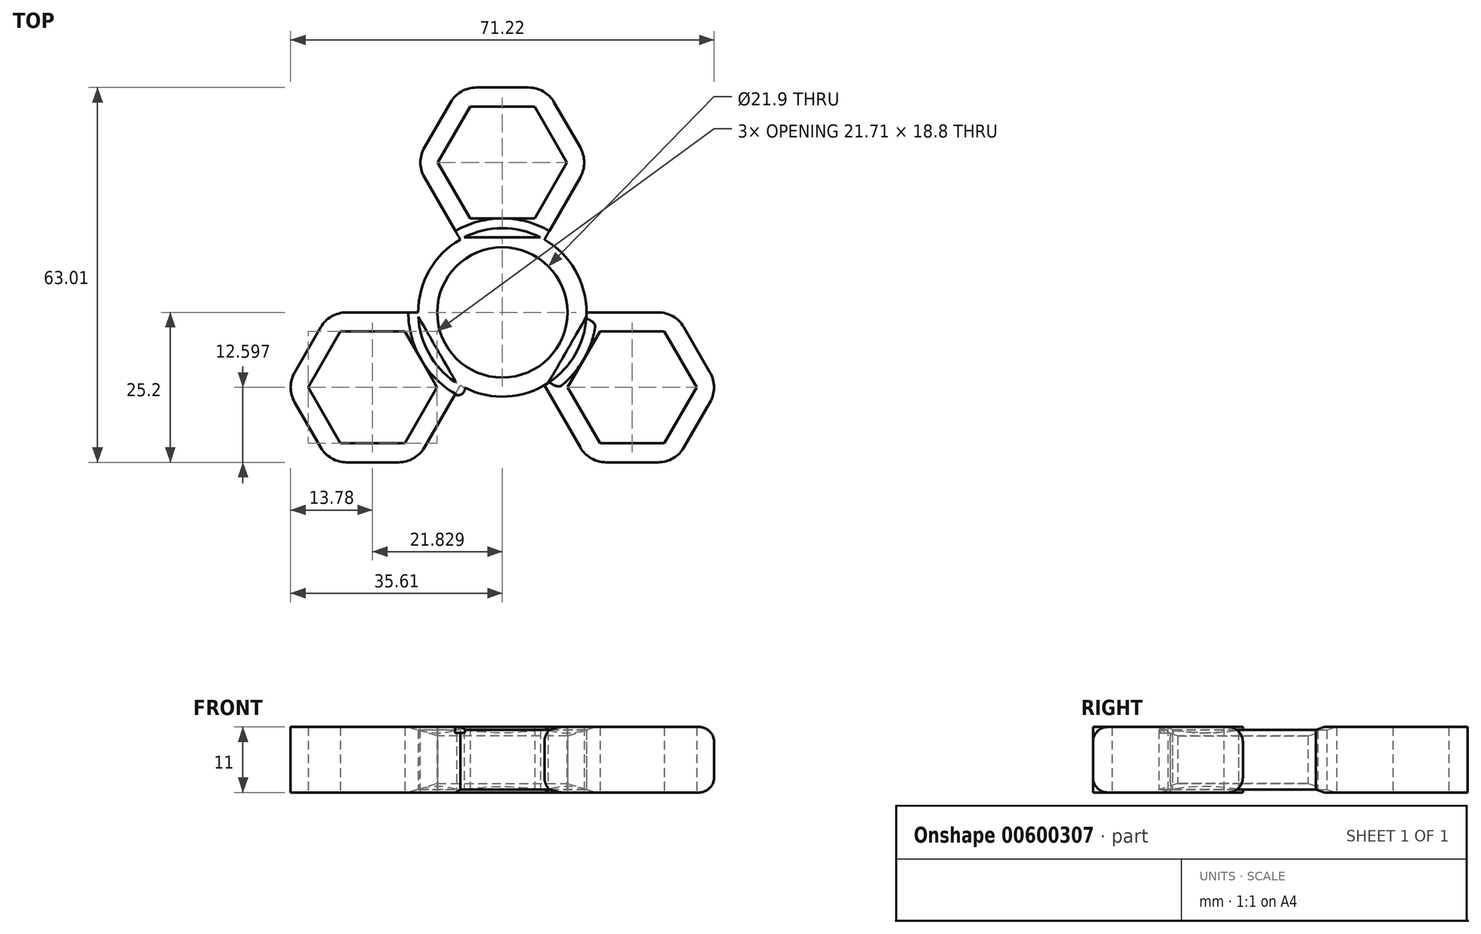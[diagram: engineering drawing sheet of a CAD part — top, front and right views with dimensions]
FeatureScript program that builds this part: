
annotation { "Feature Type Name" : "Feature", "Feature Type Description" : "" }
export const myFeature = defineFeature(function(context is Context, id is Id, definition is map)
    precondition{}
    {
        {
            var Q0;
            Q0=qCreatedBy(makeId("Top.planeOp"),FACE);
            var sketch = newSketch(context, id + "F0", { "sketchPlane" : qUnion([Q0])});
            skCircle(sketch, "E0", {"center": v(0, 0) * mm, "radius": 38.5 * mm, "construction": true});
            skLineSegment(sketch, "E1", {"start": v(0, 25.2) * mm, "end": v(0, 0) * mm, "construction": true});
            skLineSegment(sketch, "E2", {"start": v(0, 0) * mm, "end": v(-21.83, -12.6) * mm, "construction": true});
            skLineSegment(sketch, "E3", {"start": v(0, 0) * mm, "end": v(21.83, -12.6) * mm, "construction": true});
            skCircle(sketch, "E4.cCircle", {"center": v(0, 25.2) * mm, "radius": 9.4 * mm, "construction": true});
            skLineSegment(sketch, "E4.0", {"start": v(10.85, 25.2) * mm, "end": v(5.43, 15.8) * mm});
            skLineSegment(sketch, "E4.1", {"start": v(5.43, 15.8) * mm, "end": v(-5.43, 15.8) * mm});
            skLineSegment(sketch, "E4.2", {"start": v(-5.43, 15.8) * mm, "end": v(-10.85, 25.2) * mm});
            skLineSegment(sketch, "E4.3", {"start": v(-10.85, 25.2) * mm, "end": v(-5.43, 34.6) * mm});
            skLineSegment(sketch, "E4.4", {"start": v(-5.43, 34.6) * mm, "end": v(5.43, 34.6) * mm});
            skLineSegment(sketch, "E4.5", {"start": v(5.43, 34.6) * mm, "end": v(10.85, 25.2) * mm});
            skPoint(sketch, "E4.0.midPoint", {"position": v(8.14, 20.5) * mm});
            skCircle(sketch, "E5.cCircle", {"center": v(0, 25.2) * mm, "radius": 12.6 * mm, "construction": true});
            skLineSegment(sketch, "E5.0", {"start": v(14.55, 25.2) * mm, "end": v(7.27, 12.6) * mm});
            skLineSegment(sketch, "E5.1", {"start": v(7.27, 12.6) * mm, "end": v(-7.27, 12.6) * mm});
            skLineSegment(sketch, "E5.2", {"start": v(-7.27, 12.6) * mm, "end": v(-14.55, 25.2) * mm});
            skLineSegment(sketch, "E5.3", {"start": v(-14.55, 25.2) * mm, "end": v(-7.27, 37.8) * mm});
            skLineSegment(sketch, "E5.4", {"start": v(-7.27, 37.8) * mm, "end": v(7.27, 37.8) * mm});
            skLineSegment(sketch, "E5.5", {"start": v(7.27, 37.8) * mm, "end": v(14.55, 25.2) * mm});
            skPoint(sketch, "E5.0.midPoint", {"position": v(10.91, 18.9) * mm});
            skLineSegment(sketch, "E6", {"start": v(-7.27, 12.6) * mm, "end": v(-7.07, 12.26) * mm});
            skLineSegment(sketch, "E7", {"start": v(7.27, 12.6) * mm, "end": v(7.07, 12.26) * mm});
            skCircle(sketch, "E8", {"center": v(0, 0) * mm, "radius": 10.95 * mm});
            skCircle(sketch, "E9.cCircle", {"center": v(21.83, -12.6) * mm, "radius": 9.4 * mm, "construction": true});
            skLineSegment(sketch, "E9.0", {"start": v(32.68, -12.6) * mm, "end": v(27.26, -22) * mm});
            skLineSegment(sketch, "E9.1", {"start": v(27.26, -22) * mm, "end": v(16.4, -22) * mm});
            skLineSegment(sketch, "E9.2", {"start": v(16.4, -22) * mm, "end": v(10.98, -12.6) * mm});
            skLineSegment(sketch, "E9.3", {"start": v(10.98, -12.6) * mm, "end": v(16.4, -3.2) * mm});
            skLineSegment(sketch, "E9.4", {"start": v(16.4, -3.2) * mm, "end": v(27.26, -3.2) * mm});
            skLineSegment(sketch, "E9.5", {"start": v(27.26, -3.2) * mm, "end": v(32.68, -12.6) * mm});
            skPoint(sketch, "E9.0.midPoint", {"position": v(29.97, -17.3) * mm});
            skCircle(sketch, "E10.cCircle", {"center": v(21.83, -12.6) * mm, "radius": 12.6 * mm, "construction": true});
            skLineSegment(sketch, "E10.0", {"start": v(36.38, -12.6) * mm, "end": v(29.1, -25.2) * mm});
            skLineSegment(sketch, "E10.1", {"start": v(29.1, -25.2) * mm, "end": v(14.55, -25.2) * mm});
            skLineSegment(sketch, "E10.2", {"start": v(14.55, -25.2) * mm, "end": v(7.28, -12.6) * mm});
            skLineSegment(sketch, "E10.3", {"start": v(7.28, -12.6) * mm, "end": v(14.55, 0) * mm});
            skLineSegment(sketch, "E10.4", {"start": v(14.55, 0) * mm, "end": v(29.1, 0) * mm});
            skLineSegment(sketch, "E10.5", {"start": v(29.1, 0) * mm, "end": v(36.38, -12.6) * mm});
            skPoint(sketch, "E10.0.midPoint", {"position": v(32.74, -18.9) * mm});
            skCircle(sketch, "E11.cCircle", {"center": v(-21.83, -12.6) * mm, "radius": 9.4 * mm, "construction": true});
            skLineSegment(sketch, "E11.0", {"start": v(-10.98, -12.6) * mm, "end": v(-16.4, -22) * mm});
            skLineSegment(sketch, "E11.1", {"start": v(-16.4, -22) * mm, "end": v(-27.26, -22) * mm});
            skLineSegment(sketch, "E11.2", {"start": v(-27.26, -22) * mm, "end": v(-32.68, -12.6) * mm});
            skLineSegment(sketch, "E11.3", {"start": v(-32.68, -12.6) * mm, "end": v(-27.26, -3.2) * mm});
            skLineSegment(sketch, "E11.4", {"start": v(-27.26, -3.2) * mm, "end": v(-16.4, -3.2) * mm});
            skLineSegment(sketch, "E11.5", {"start": v(-16.4, -3.2) * mm, "end": v(-10.98, -12.6) * mm});
            skPoint(sketch, "E11.0.midPoint", {"position": v(-13.69, -17.3) * mm});
            skCircle(sketch, "E12.cCircle", {"center": v(-21.83, -12.6) * mm, "radius": 12.6 * mm, "construction": true});
            skLineSegment(sketch, "E12.0", {"start": v(-7.28, -12.6) * mm, "end": v(-14.55, -25.2) * mm});
            skLineSegment(sketch, "E12.1", {"start": v(-14.55, -25.2) * mm, "end": v(-29.1, -25.2) * mm});
            skLineSegment(sketch, "E12.2", {"start": v(-29.1, -25.2) * mm, "end": v(-36.38, -12.6) * mm});
            skLineSegment(sketch, "E12.3", {"start": v(-36.38, -12.6) * mm, "end": v(-29.1, 0) * mm});
            skLineSegment(sketch, "E12.4", {"start": v(-29.1, 0) * mm, "end": v(-14.55, 0) * mm});
            skLineSegment(sketch, "E12.5", {"start": v(-14.55, 0) * mm, "end": v(-7.28, -12.6) * mm});
            skPoint(sketch, "E12.0.midPoint", {"position": v(-10.92, -18.9) * mm});
            skLineSegment(sketch, "E13", {"start": v(-14.55, 0) * mm, "end": v(-14.15, 0) * mm});
            skLineSegment(sketch, "E14", {"start": v(-7.28, -12.6) * mm, "end": v(-7.08, -12.25) * mm});
            skLineSegment(sketch, "E15", {"start": v(7.28, -12.6) * mm, "end": v(7.08, -12.25) * mm});
            skLineSegment(sketch, "E16", {"start": v(14.55, 0) * mm, "end": v(14.15, 0) * mm});
            skCircle(sketch, "E17", {"center": v(0, 0) * mm, "radius": 14.15 * mm});
            skSolve(sketch);
        }
        {
            var Q0;
            Q0=qSketchRegion(id+"F0",true);
            extrude(context, id + "F1", {"entities" : qUnion([Q0]), "endBound" : BoundingType.SYMMETRIC, "depth" : 11 * mm, "offsetDistance" : 25 * mm});
        }
        {
            var Q0;
            Q0=makeQuery(id+"F1.opExtrude","CAP_FACE",FACE,{"disambiguationData":[OSD([sQuery(id+"F0.wireOp",EDGE,"E4.0"),sQuery(id+"F0.wireOp",EDGE,"E4.1"),sQuery(id+"F0.wireOp",EDGE,"E4.2"),sQuery(id+"F0.wireOp",EDGE,"E4.3"),sQuery(id+"F0.wireOp",EDGE,"E4.4"),sQuery(id+"F0.wireOp",EDGE,"E4.5"),sQuery(id+"F0.wireOp",EDGE,"E5.0"),sQuery(id+"F0.wireOp",EDGE,"E5.2"),sQuery(id+"F0.wireOp",EDGE,"E5.3"),sQuery(id+"F0.wireOp",EDGE,"E5.4"),sQuery(id+"F0.wireOp",EDGE,"E5.5"),sQuery(id+"F0.wireOp",EDGE,"E8"),sQuery(id+"F0.wireOp",EDGE,"E9.0"),sQuery(id+"F0.wireOp",EDGE,"E9.1"),sQuery(id+"F0.wireOp",EDGE,"E9.2"),sQuery(id+"F0.wireOp",EDGE,"E9.3"),sQuery(id+"F0.wireOp",EDGE,"E9.4"),sQuery(id+"F0.wireOp",EDGE,"E9.5"),sQuery(id+"F0.wireOp",EDGE,"E10.0"),sQuery(id+"F0.wireOp",EDGE,"E10.1"),sQuery(id+"F0.wireOp",EDGE,"E10.2"),sQuery(id+"F0.wireOp",EDGE,"E10.4"),sQuery(id+"F0.wireOp",EDGE,"E10.5"),sQuery(id+"F0.wireOp",EDGE,"E11.0"),sQuery(id+"F0.wireOp",EDGE,"E11.1"),sQuery(id+"F0.wireOp",EDGE,"E11.2"),sQuery(id+"F0.wireOp",EDGE,"E11.3"),sQuery(id+"F0.wireOp",EDGE,"E11.4"),sQuery(id+"F0.wireOp",EDGE,"E11.5"),sQuery(id+"F0.wireOp",EDGE,"E12.0"),sQuery(id+"F0.wireOp",EDGE,"E12.1"),sQuery(id+"F0.wireOp",EDGE,"E12.2"),sQuery(id+"F0.wireOp",EDGE,"E12.3"),sQuery(id+"F0.wireOp",EDGE,"E12.4"),sQuery(id+"F0.wireOp",EDGE,"E17")])],"isStart":false});
            var sketch = newSketch(context, id + "F2", { "sketchPlane" : qUnion([Q0])});
            skCircle(sketch, "E18", {"center": v(-7.49, -12.72) * mm, "radius": 1.2 * mm});
            skSolve(sketch);
        }
        {
            var Q0;
            Q0 = qSketchRegion(id + "F2", true);
            extrude(context, id + "F3", {"entities" : qUnion([Q0]), "operationType" : NewBodyOperationType.ADD, "oppositeDirection" : true, "depth" : 1 * mm, "offsetDistance" : 25 * mm});
        }
        {
            var Q0;
            Q0=qCreatedBy(makeId("Right.planeOp"),FACE);
            var sketch = newSketch(context, id + "F4", { "sketchPlane" : qUnion([Q0])});
            skLineSegment(sketch, "E19", {"start": v(-10.95, -5.5) * mm, "end": v(-10.95, 5.5) * mm, "construction": true});
            skLineSegment(sketch, "E20", {"start": v(10.95, 5.5) * mm, "end": v(10.95, -5.5) * mm, "construction": true});
            skLineSegment(sketch, "E21.0.0", {"start": v(15.8, -5.5) * mm, "end": v(25.2, -5.5) * mm, "construction": true});
            skLineSegment(sketch, "E21.0.1", {"start": v(25.2, -5.5) * mm, "end": v(25.2, 5.5) * mm, "construction": true});
            skLineSegment(sketch, "E21.0.2", {"start": v(25.2, 5.5) * mm, "end": v(15.8, 5.5) * mm, "construction": true});
            skLineSegment(sketch, "E21.0.3", {"start": v(15.8, 5.5) * mm, "end": v(15.8, -5.5) * mm, "construction": true});
            skLineSegment(sketch, "E22", {"start": v(10.95, 4) * mm, "end": v(15.8, 5.5) * mm});
            skLineSegment(sketch, "E23", {"start": v(15.8, 5.5) * mm, "end": v(10.95, 5.5) * mm});
            skLineSegment(sketch, "E24", {"start": v(10.95, 5.5) * mm, "end": v(10.95, 4) * mm});
            skLineSegment(sketch, "E25", {"start": v(10.95, -4) * mm, "end": v(10.95, -5.5) * mm});
            skLineSegment(sketch, "E26", {"start": v(10.95, -5.5) * mm, "end": v(15.8, -5.5) * mm});
            skLineSegment(sketch, "E27", {"start": v(15.8, -5.5) * mm, "end": v(10.95, -4) * mm});
            skLineSegment(sketch, "E28", {"start": v(0, 0) * mm, "end": v(0, 13.53) * mm, "construction": true});
            skSolve(sketch);
        }
        {
            var Q0;
            Q0=qSketchRegion(id+"F4",true);
            var Q1;
            Q1=sQuery(id+"F4.wireOp",EDGE,"E28");
            revolve(context, id + "F5", {"operationType" : NewBodyOperationType.REMOVE, "surfaceOperationType" : NewSurfaceOperationType.NEW, "entities" : qUnion([Q0]), "axis" : qUnion([Q1]), "revolveType" : RevolveType.FULL, "oppositeDirection" : true});
        }
        {
            var Q0;
            Q0=makeQuery(id+"F3.boolean.opBoolean","MERGE",EDGE,{"derivedFrom":[makeQuery(id+"F1.opExtrude","SWEPT_EDGE",EDGE,{"disambiguationData":[OSD([sQuery(id+"F0.wireOp",EDGE,"E10.4"),sQuery(id+"F0.wireOp",EDGE,"E10.5")])]}),makeQuery(id+"FbIfJMkWUXHlg3o_1.1.F1.opExtrude","SWEPT_EDGE",EDGE,{"disambiguationData":[OSD([sQuery(id+"F0.wireOp",EDGE,"E12.3"),sQuery(id+"F0.wireOp",EDGE,"E12.4")])]})]});
            var Q1;
            Q1=makeQuery(id+"FbIfJMkWUXHlg3o_1.1.F1.opExtrude","SWEPT_EDGE",EDGE,{"disambiguationData":[OSD([sQuery(id+"F0.wireOp",EDGE,"E12.2"),sQuery(id+"F0.wireOp",EDGE,"E12.3")])]});
            var Q2;
            Q2=makeQuery(id+"FbIfJMkWUXHlg3o_1.1.F1.opExtrude","SWEPT_EDGE",EDGE,{"disambiguationData":[OSD([sQuery(id+"F0.wireOp",EDGE,"E12.1"),sQuery(id+"F0.wireOp",EDGE,"E12.2")])]});
            var Q3;
            Q3=makeQuery(id+"F3.boolean.opBoolean","MERGE",EDGE,{"derivedFrom":[makeQuery(id+"F1.opExtrude","SWEPT_EDGE",EDGE,{"disambiguationData":[OSD([sQuery(id+"F0.wireOp",EDGE,"E5.0"),sQuery(id+"F0.wireOp",EDGE,"E5.5")])]}),makeQuery(id+"FbIfJMkWUXHlg3o_1.1.F1.opExtrude","SWEPT_EDGE",EDGE,{"disambiguationData":[OSD([sQuery(id+"F0.wireOp",EDGE,"E12.0"),sQuery(id+"F0.wireOp",EDGE,"E12.1")])]})]});
            var Q4;
            Q4=makeQuery(id+"F1.opExtrude","SWEPT_EDGE",EDGE,{"disambiguationData":[OSD([sQuery(id+"F0.wireOp",EDGE,"E5.4"),sQuery(id+"F0.wireOp",EDGE,"E5.5")])]});
            var Q5;
            Q5=makeQuery(id+"F1.opExtrude","SWEPT_EDGE",EDGE,{"disambiguationData":[OSD([sQuery(id+"F0.wireOp",EDGE,"E5.3"),sQuery(id+"F0.wireOp",EDGE,"E5.4")])]});
            var Q6;
            Q6=makeQuery(id+"FbIfJMkWUXHlg3o_1.1.F1.opExtrude","SWEPT_EDGE",EDGE,{"disambiguationData":[OSD([sQuery(id+"F0.wireOp",EDGE,"E10.0"),sQuery(id+"F0.wireOp",EDGE,"E10.1")])]});
            var Q7;
            Q7=makeQuery(id+"F3.boolean.opBoolean","MERGE",EDGE,{"derivedFrom":[makeQuery(id+"F1.opExtrude","SWEPT_EDGE",EDGE,{"disambiguationData":[OSD([sQuery(id+"F0.wireOp",EDGE,"E5.2"),sQuery(id+"F0.wireOp",EDGE,"E5.3")])]}),makeQuery(id+"FbIfJMkWUXHlg3o_1.1.F1.opExtrude","SWEPT_EDGE",EDGE,{"disambiguationData":[OSD([sQuery(id+"F0.wireOp",EDGE,"E10.1"),sQuery(id+"F0.wireOp",EDGE,"E10.2")])]})]});
            var Q8;
            Q8=makeQuery(id+"FbIfJMkWUXHlg3o_1.1.F1.opExtrude","SWEPT_EDGE",EDGE,{"disambiguationData":[OSD([sQuery(id+"F0.wireOp",EDGE,"E10.0"),sQuery(id+"F0.wireOp",EDGE,"E10.5")])]});
            var Q9;
            Q9=makeQuery(id+"F3.boolean.opBoolean","MERGE",EDGE,{"derivedFrom":[makeQuery(id+"F1.opExtrude","SWEPT_EDGE",EDGE,{"disambiguationData":[OSD([sQuery(id+"F0.wireOp",EDGE,"E12.3"),sQuery(id+"F0.wireOp",EDGE,"E12.4")])]}),makeQuery(id+"FbIfJMkWUXHlg3o_1.1.F1.opExtrude","SWEPT_EDGE",EDGE,{"disambiguationData":[OSD([sQuery(id+"F0.wireOp",EDGE,"E10.4"),sQuery(id+"F0.wireOp",EDGE,"E10.5")])]})]});
            var Q10;
            Q10=makeQuery(id+"F1.opExtrude","SWEPT_EDGE",EDGE,{"disambiguationData":[OSD([sQuery(id+"F0.wireOp",EDGE,"E12.2"),sQuery(id+"F0.wireOp",EDGE,"E12.3")])]});
            var Q11;
            Q11=makeQuery(id+"F1.opExtrude","SWEPT_EDGE",EDGE,{"disambiguationData":[OSD([sQuery(id+"F0.wireOp",EDGE,"E12.1"),sQuery(id+"F0.wireOp",EDGE,"E12.2")])]});
            var Q12;
            Q12=makeQuery(id+"F3.boolean.opBoolean","MERGE",EDGE,{"derivedFrom":[makeQuery(id+"F1.opExtrude","SWEPT_EDGE",EDGE,{"disambiguationData":[OSD([sQuery(id+"F0.wireOp",EDGE,"E12.0"),sQuery(id+"F0.wireOp",EDGE,"E12.1")])]}),makeQuery(id+"FbIfJMkWUXHlg3o_1.1.F1.opExtrude","SWEPT_EDGE",EDGE,{"disambiguationData":[OSD([sQuery(id+"F0.wireOp",EDGE,"E5.0"),sQuery(id+"F0.wireOp",EDGE,"E5.5")])]})]});
            var Q13;
            Q13=makeQuery(id+"FbIfJMkWUXHlg3o_1.1.F1.opExtrude","SWEPT_EDGE",EDGE,{"disambiguationData":[OSD([sQuery(id+"F0.wireOp",EDGE,"E5.4"),sQuery(id+"F0.wireOp",EDGE,"E5.5")])]});
            var Q14;
            Q14=makeQuery(id+"F1.opExtrude","SWEPT_EDGE",EDGE,{"disambiguationData":[OSD([sQuery(id+"F0.wireOp",EDGE,"E10.0"),sQuery(id+"F0.wireOp",EDGE,"E10.5")])]});
            var Q15;
            Q15=makeQuery(id+"F1.opExtrude","SWEPT_EDGE",EDGE,{"disambiguationData":[OSD([sQuery(id+"F0.wireOp",EDGE,"E10.0"),sQuery(id+"F0.wireOp",EDGE,"E10.1")])]});
            var Q16;
            Q16=makeQuery(id+"F3.boolean.opBoolean","MERGE",EDGE,{"derivedFrom":[makeQuery(id+"F1.opExtrude","SWEPT_EDGE",EDGE,{"disambiguationData":[OSD([sQuery(id+"F0.wireOp",EDGE,"E10.1"),sQuery(id+"F0.wireOp",EDGE,"E10.2")])]}),makeQuery(id+"FbIfJMkWUXHlg3o_1.1.F1.opExtrude","SWEPT_EDGE",EDGE,{"disambiguationData":[OSD([sQuery(id+"F0.wireOp",EDGE,"E5.2"),sQuery(id+"F0.wireOp",EDGE,"E5.3")])]})]});
            var Q17;
            Q17=makeQuery(id+"FbIfJMkWUXHlg3o_1.1.F1.opExtrude","SWEPT_EDGE",EDGE,{"disambiguationData":[OSD([sQuery(id+"F0.wireOp",EDGE,"E5.3"),sQuery(id+"F0.wireOp",EDGE,"E5.4")])]});
            fillet(context, id + "F6", {"entities" : qUnion([Q0, Q1, Q2, Q3, Q4, Q5, Q6, Q7, Q8, Q9, Q10, Q11, Q12, Q13, Q14, Q15, Q16, Q17]), "radius" : 5 * mm, "tangentPropagation" : true, "allowEdgeOverflow" : false});
        }
        {
            var Q0;
            Q0=makeQuery(id+"F1.opExtrude","CAP_EDGE",EDGE,{"disambiguationData":[OSD([sQuery(id+"F0.wireOp",EDGE,"E10.5")])],"isStart":false});
            var Q1;
            Q1=makeQuery(id+"F1.opExtrude","CAP_EDGE",EDGE,{"disambiguationData":[OSD([sQuery(id+"F0.wireOp",EDGE,"E10.5")])],"isStart":true});
            fillet(context, id + "F7", {"entities" : qUnion([Q0, Q1]), "radius" : 2.5 * mm, "tangentPropagation" : true, "allowEdgeOverflow" : false});
        }
    });
